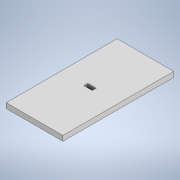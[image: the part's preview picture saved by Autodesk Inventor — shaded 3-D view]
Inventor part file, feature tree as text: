
AUTODESK INVENTOR PART (.ipt)
format: ipt  version: 2022.1 (Build 261234020, 234B)  size: 230,400 bytes
history: native  units: mm
features: extrude x1, sketch x1
ambient origin geometry x8: Origin, YZ Plane, XZ Plane, XY Plane, X Axis, Y Axis, Z Axis, Center Point
bodies: Solid1 (feature_tree)
feature tree (2):
  extrude  "Extrusion1"  Depth=215.0mm
  sketch  "Sketch1"  dims[d0=110.0mm d1=215.0mm d2=10.0mm d3=0.0mm d4=103.75676mm d6=15.927307mm d7=47.036347mm d8=7.48648mm]
